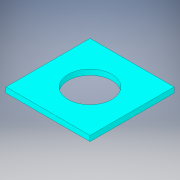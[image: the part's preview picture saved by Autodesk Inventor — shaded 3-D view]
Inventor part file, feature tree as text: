
AUTODESK INVENTOR PART (.ipt)
format: ipt  version: 2019 (Build 230136000, 136)  size: 110,592 bytes
history: native  units: mm
features: extrude x1, sketch x1
ambient origin geometry x8: Origin, YZ Plane, XZ Plane, XY Plane, X Axis, Y Axis, Z Axis, Center Point
bodies: Solid1 (feature_tree)
feature tree (2):
  extrude  "Extrusion1"  Depth=50.0mm
  sketch  "Sketch1"  dims[d0=50.0mm d1=50.0mm d2=26.0mm d3=3.18mm d4=0.0mm]
